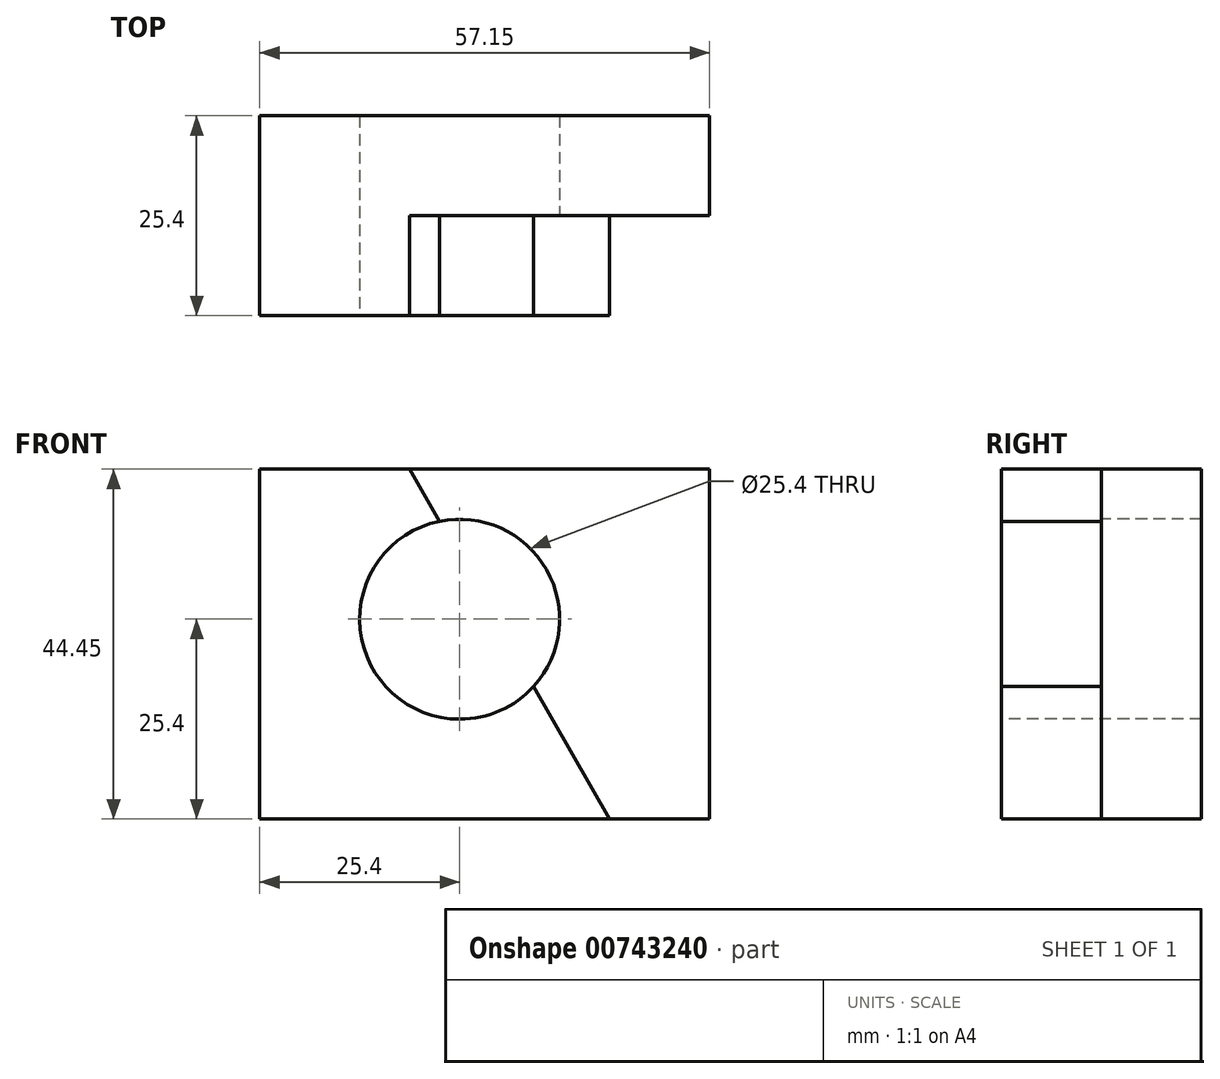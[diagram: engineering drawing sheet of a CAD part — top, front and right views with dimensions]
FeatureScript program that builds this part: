
annotation { "Feature Type Name" : "Feature", "Feature Type Description" : "" }
export const myFeature = defineFeature(function(context is Context, id is Id, definition is map)
    precondition{}
    {
        {
            var Q0;
            Q0=qCreatedBy(makeId("Front.planeOp"),FACE);
            var sketch = newSketch(context, id + "F0", { "sketchPlane" : qUnion([Q0])});
            skLineSegment(sketch, "E0.bottom", {"start": v(0, 0) * mm, "end": v(57.15, 0) * mm});
            skLineSegment(sketch, "E0.top", {"start": v(0, 44.45) * mm, "end": v(57.15, 44.45) * mm});
            skLineSegment(sketch, "E0.left", {"start": v(0, 0) * mm, "end": v(0, 44.45) * mm});
            skLineSegment(sketch, "E0.right", {"start": v(57.15, 0) * mm, "end": v(57.15, 44.45) * mm});
            skSolve(sketch);
        }
        {
            var Q0;
            Q0=makeQuery(id+"F0.imprint","IMPRINT",FACE,{"disambiguationData":[TD([[makeQuery(id+"F0.imprint","IMPRINT",EDGE,{"derivedFrom":sQuery(id+"F0.wireOp",EDGE,"E0.bottom")}),1.0]])]});
            extrude(context, id + "F1", {"entities" : qUnion([Q0]), "depth" : 25.4 * mm, "offsetDistance" : 25.4 * mm});
        }
        {
            var Q0;
            Q0=makeQuery(id+"F1.opExtrude","CAP_FACE",FACE,{"disambiguationData":[OSD([sQuery(id+"F0.wireOp",EDGE,"E0.bottom"),sQuery(id+"F0.wireOp",EDGE,"E0.top"),sQuery(id+"F0.wireOp",EDGE,"E0.left"),sQuery(id+"F0.wireOp",EDGE,"E0.right")])],"isStart":false});
            var sketch = newSketch(context, id + "F2", { "sketchPlane" : qUnion([Q0])});
            skCircle(sketch, "E1", {"center": v(25.4, 25.4) * mm, "radius": 12.7 * mm});
            skSolve(sketch);
        }
        {
            var Q0;
            Q0=makeQuery(id+"F2.imprint","IMPRINT",FACE,{"disambiguationData":[TD([[makeQuery(id+"F2.imprint","IMPRINT",EDGE,{"derivedFrom":sQuery(id+"F2.wireOp",EDGE,"E1")}),1.0]])]});
            extrude(context, id + "F3", {"entities" : qUnion([Q0]), "operationType" : NewBodyOperationType.REMOVE, "oppositeDirection" : true, "depth" : 25.4 * mm, "offsetDistance" : 25.4 * mm});
        }
        {
            var Q0;
            Q0=makeQuery(id+"F1.opExtrude","CAP_FACE",FACE,{"disambiguationData":[OSD([sQuery(id+"F0.wireOp",EDGE,"E0.bottom"),sQuery(id+"F0.wireOp",EDGE,"E0.top"),sQuery(id+"F0.wireOp",EDGE,"E0.left"),sQuery(id+"F0.wireOp",EDGE,"E0.right")])],"isStart":false});
            var sketch = newSketch(context, id + "F4", { "sketchPlane" : qUnion([Q0])});
            skLineSegment(sketch, "E2", {"start": v(19.05, 44.45) * mm, "end": v(44.45, 0) * mm});
            skLineSegment(sketch, "E3", {"start": v(44.45, 0) * mm, "end": v(57.15, 0) * mm});
            skLineSegment(sketch, "E4", {"start": v(57.15, 0) * mm, "end": v(57.15, 44.45) * mm});
            skLineSegment(sketch, "E5", {"start": v(57.15, 44.45) * mm, "end": v(19.05, 44.45) * mm});
            skSolve(sketch);
        }
        {
            var Q0;
            {var subQ0=sQuery(id+"F4.wireOp",EDGE,"E3");Q0=makeQuery(id+"F4.imprint","IMPRINT",FACE,{"disambiguationData":[TD([[makeQuery(id+"F4.imprint","IMPRINT",EDGE,{"derivedFrom":subQ0}),1.0]])]});}
            extrude(context, id + "F5", {"entities" : qUnion([Q0]), "operationType" : NewBodyOperationType.REMOVE, "oppositeDirection" : true, "depth" : 12.7 * mm, "offsetDistance" : 25.4 * mm});
        }
    });
